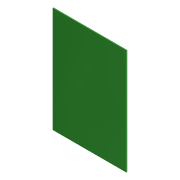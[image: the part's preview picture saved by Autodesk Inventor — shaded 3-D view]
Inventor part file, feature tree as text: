
AUTODESK INVENTOR PART (.ipt)
format: ipt  version: 2022 (Build 260153000, 153)  size: 74,752 bytes
history: native  units: mm
features: extrude x1, sketch x1
ambient origin geometry x8: Origin, YZ Plane, XZ Plane, XY Plane, X Axis, Y Axis, Z Axis, Center Point
bodies: Volumenkörper1 (feature_tree)
feature tree (2):
  extrude  "Extrusion1"  [1 undecoded]
  sketch  "Skizze1"  dims[d0=1.0mm d1=0.0mm]
note: 1 required parameter value undecoded (feature->parameter linkage not recoverable at this tier; creation-order binding heuristic only, values carry confidence <= 0.55)
